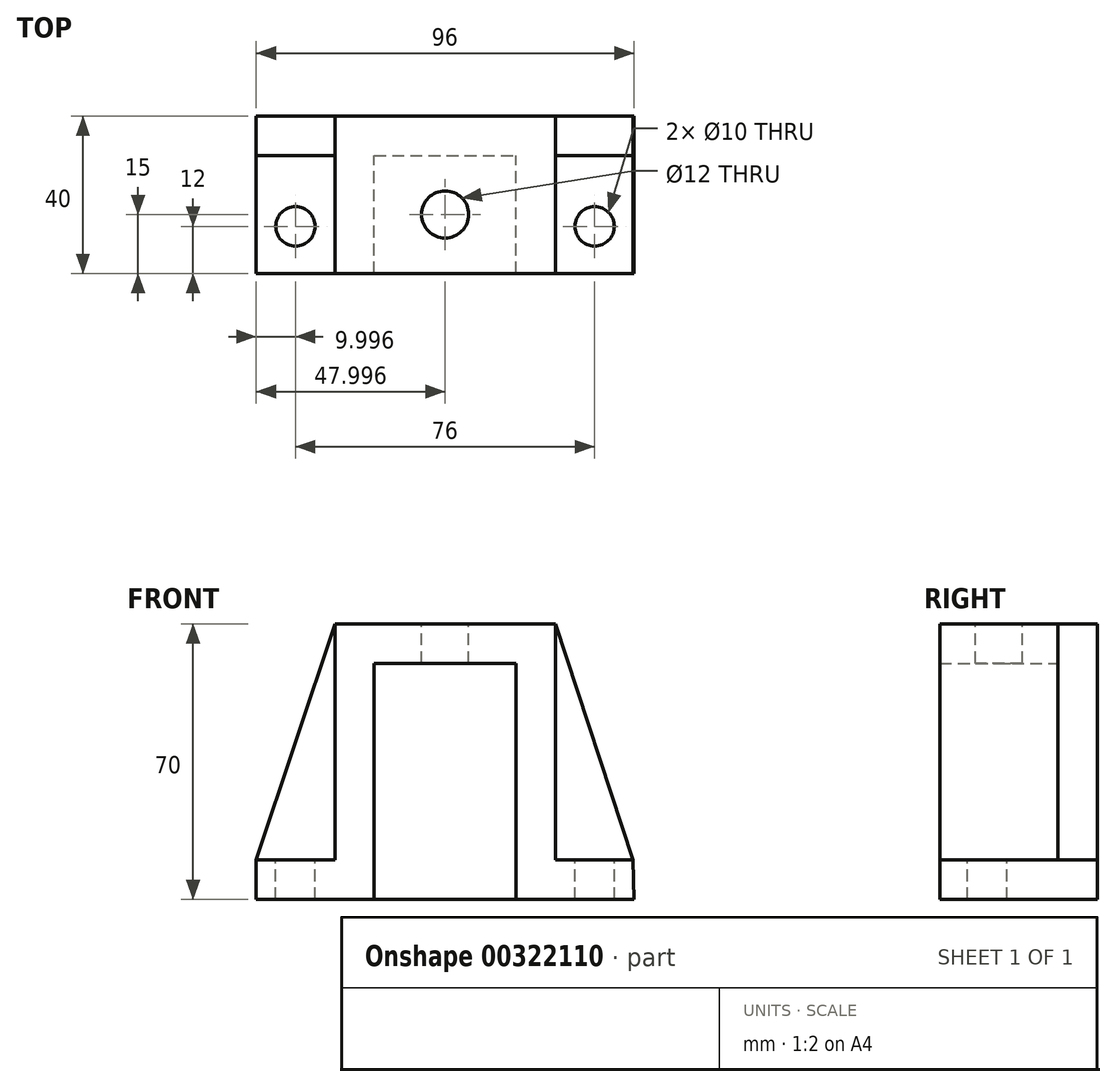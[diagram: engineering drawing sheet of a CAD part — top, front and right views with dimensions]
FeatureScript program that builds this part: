
annotation { "Feature Type Name" : "Feature", "Feature Type Description" : "" }
export const myFeature = defineFeature(function(context is Context, id is Id, definition is map)
    precondition{}
    {
        {
            var Q0;
            Q0=qCreatedBy(makeId("Front.planeOp"),FACE);
            var sketch = newSketch(context, id + "F0", { "sketchPlane" : qUnion([Q0])});
            skLineSegment(sketch, "E0", {"start": v(-53.16, -16.87) * mm, "end": v(42.84, -16.87) * mm});
            skLineSegment(sketch, "E1", {"start": v(-53.16, -16.87) * mm, "end": v(-53.16, -6.87) * mm});
            skLineSegment(sketch, "E2", {"start": v(-53.16, -6.87) * mm, "end": v(-33.16, -6.87) * mm});
            skLineSegment(sketch, "E3", {"start": v(-33.16, -6.87) * mm, "end": v(-33.16, 53.13) * mm});
            skLineSegment(sketch, "E4", {"start": v(-33.16, 53.13) * mm, "end": v(22.84, 53.13) * mm});
            skLineSegment(sketch, "E5", {"start": v(22.84, 53.13) * mm, "end": v(22.84, -6.87) * mm});
            skLineSegment(sketch, "E6", {"start": v(22.84, -6.87) * mm, "end": v(42.61, -6.87) * mm});
            skLineSegment(sketch, "E7", {"start": v(42.61, -6.87) * mm, "end": v(42.84, -16.87) * mm});
            skLineSegment(sketch, "E8", {"start": v(-33.16, 53.13) * mm, "end": v(-53.16, -6.87) * mm});
            skLineSegment(sketch, "E9", {"start": v(22.84, 53.13) * mm, "end": v(42.61, -6.87) * mm});
            skLineSegment(sketch, "E10", {"start": v(-23.16, -16.87) * mm, "end": v(-23.16, 43.13) * mm});
            skLineSegment(sketch, "E11", {"start": v(-23.16, 43.13) * mm, "end": v(12.84, 43.13) * mm});
            skLineSegment(sketch, "E12", {"start": v(12.84, 43.13) * mm, "end": v(12.84, -16.87) * mm});
            skSolve(sketch);
        }
        {
            var Q0;
            {var subQ2=sQuery(id+"F0.wireOp",EDGE,"E1");Q0=makeQuery(id+"F0.imprint","IMPRINT",FACE,{"disambiguationData":[TD([[makeQuery(id+"F0.imprint","IMPRINT",EDGE,{"derivedFrom":subQ2}),-1.0]])]});}
            extrude(context, id + "F1", {"entities" : qUnion([Q0]), "depth" : 40 * mm});
        }
        {
            var Q0;
            {var subQ0=sQuery(id+"F0.wireOp",EDGE,"E10");Q0=makeQuery(id+"F0.imprint","IMPRINT",FACE,{"disambiguationData":[TD([[makeQuery(id+"F0.imprint","IMPRINT",EDGE,{"derivedFrom":subQ0}),-1.0]])]});}
            extrude(context, id + "F2", {"entities" : qUnion([Q0]), "operationType" : NewBodyOperationType.ADD, "depth" : 10 * mm});
        }
        {
            var Q0;
            Q0=makeQuery(id+"F0.imprint","IMPRINT",FACE,{"disambiguationData":[TD([[makeQuery(id+"F0.imprint","IMPRINT",EDGE,{"derivedFrom":sQuery(id+"F0.wireOp",EDGE,"E2")}),1.0]])]});
            var Q1;
            Q1=makeQuery(id+"F0.imprint","IMPRINT",FACE,{"disambiguationData":[TD([[makeQuery(id+"F0.imprint","IMPRINT",EDGE,{"derivedFrom":sQuery(id+"F0.wireOp",EDGE,"E5")}),1.0]])]});
            extrude(context, id + "F3", {"entities" : qUnion([Q0, Q1]), "operationType" : NewBodyOperationType.ADD, "depth" : 10 * mm});
        }
        {
            var Q0;
            Q0=makeQuery(id+"F1.opExtrude","SWEPT_FACE",FACE,{"disambiguationData":[OSD([sQuery(id+"F0.wireOp",EDGE,"E4")])]});
            var sketch = newSketch(context, id + "F4", { "sketchPlane" : qUnion([Q0])});
            skLineSegment(sketch, "E13", {"start": v(-5.16, 0) * mm, "end": v(-5.16, -25) * mm, "construction": true});
            skLineSegment(sketch, "E14", {"start": v(-33.16, -25) * mm, "end": v(22.84, -25) * mm, "construction": true});
            skCircle(sketch, "E15", {"center": v(-5.16, -25) * mm, "radius": 6 * mm});
            skLineSegment(sketch, "E16.trimOffspring", {"start": v(-5.16, -28) * mm, "end": v(-5.16, -40) * mm, "construction": true});
            skLineSegment(sketch, "E17", {"start": v(22.84, -40) * mm, "end": v(32.84, -40) * mm});
            skLineSegment(sketch, "E18", {"start": v(-5.16, -25) * mm, "end": v(-5.16, -28) * mm, "construction": true});
            skLineSegment(sketch, "E19.MirrorCS", {"start": v(-43.16, -40) * mm, "end": v(-43.16, -33) * mm});
            skCircle(sketch, "E20", {"center": v(32.84, -28) * mm, "radius": 5 * mm});
            skCircle(sketch, "E21", {"center": v(-43.16, -28) * mm, "radius": 5 * mm});
            skPoint(sketch, "E22.orphan", {"position": v(32.84, -10.42) * mm});
            skPoint(sketch, "E23.orphan", {"position": v(-43.16, -10.42) * mm});
            skSolve(sketch);
        }
        {
            var Q0;
            Q0=makeQuery(id+"F4.imprint","IMPRINT",FACE,{"disambiguationData":[TD([[makeQuery(id+"F4.imprint","IMPRINT",EDGE,{"derivedFrom":sQuery(id+"F4.wireOp",EDGE,"E15")}),1.0]])]});
            extrude(context, id + "F5", {"entities" : qUnion([Q0]), "operationType" : NewBodyOperationType.REMOVE, "oppositeDirection" : true, "depth" : 25 * mm});
        }
        {
            var Q0;
            Q0=makeQuery(id+"F4.imprint","IMPRINT",FACE,{"disambiguationData":[TD([[makeQuery(id+"F4.imprint","IMPRINT",EDGE,{"derivedFrom":sQuery(id+"F4.wireOp",EDGE,"E20")}),1.0]])]});
            var Q1;
            Q1=makeQuery(id+"F4.imprint","IMPRINT",FACE,{"disambiguationData":[TD([[makeQuery(id+"F4.imprint","IMPRINT",EDGE,{"derivedFrom":sQuery(id+"F4.wireOp",EDGE,"E21")}),1.0]])]});
            extrude(context, id + "F6", {"entities" : qUnion([Q0, Q1]), "operationType" : NewBodyOperationType.REMOVE, "oppositeDirection" : true, "depth" : 70 * mm});
        }
    });
